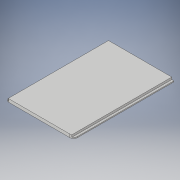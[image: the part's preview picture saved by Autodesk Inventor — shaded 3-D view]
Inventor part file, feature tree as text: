
AUTODESK INVENTOR PART (.ipt)
format: ipt  version: 2018 (Build 220112000, 112)  size: 164,352 bytes
history: native  units: in
note: dims shown in document units (in); Inventor stores cm internally (conversion verified against a paired STEP export)
features: extrude x5, sketch x5, projected_geometry x1
ambient origin geometry x8: Origin, YZ Plane, XZ Plane, XY Plane, X Axis, Y Axis, Z Axis, Center Point
bodies: Solid1 (feature_tree)
feature tree (11):
  extrude  "Extrusion1"  Depth=5.053in TaperAngle=0.0deg
  extrude  "Extrusion2"  Depth=0.1969in
  extrude  "Extrusion3"  Depth=5.053in
  extrude  "Extrusion4"  Depth=0.0295in TaperAngle=0.0deg
  extrude  "Extrusion5"  Depth=1.3in
  sketch  "Sketch1"  dims[d0=0.1575in d1=0.0787in d2=0.0787in d3=5.053in d4=0.0in]
  sketch  "Sketch3"  dims[d5=0.125in d6=0.1969in]
  sketch  "Sketch4"  dims[d7=5.053in d8=0.0in d9=0.0295in]
  sketch  "Sketch5"  dims[d10=0.0295in d11=0.0295in d12=1.0in d13=0.0in d14=0.0in]
  sketch  "Sketch6"  dims[d15=0.22in d16=1.3in d17=1.3in d18=0.1181in d19=0.0394in d20=0.0in d21=0.1575in d22=0.5512in d23=0.1575in d24=0.0689in d25=0.0in]
  projected_geometry  "Projected Loop1"
